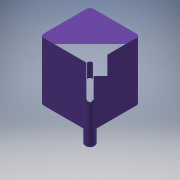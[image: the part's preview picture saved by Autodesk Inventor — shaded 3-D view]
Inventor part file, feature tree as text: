
AUTODESK INVENTOR PART (.ipt)
format: ipt  version: 2016 (Build 200138000, 138)  size: 137,216 bytes
history: native  units: mm
features: extrude x3, sketch x3, other x1, hole x1, chamfer x1, fillet x1
ambient origin geometry x8: Origin, YZ Plane, XZ Plane, XY Plane, X Axis, Y Axis, Z Axis, Center Point
bodies: Solid1 (feature_tree)
feature tree (10):
  other  "Fixture.ipt"
  extrude  "Extrusion1"  Depth=28.3mm
  hole  "Hole2"  [1 undecoded]
  sketch  "Sketch3"  dims[d3=51.0mm d4=0.0mm d12=2.0mm d13=0.0mm]
  extrude  "Extrusion2"  Depth=2.0mm TaperAngle=45.0deg
  extrude  "Extrusion3"  Depth=2.16mm
  chamfer  "Chamfer1"  Distance=10.0mm
  fillet  "Fillet1"  Radius=23.0mm
  sketch  "Sketch1"  dims[d0=28.3mm d2=22.0mm]
  sketch  "Sketch4"  dims[d15=20.0mm d16=0.0mm d17=0.6mm d18=2.0mm d19=45.0deg d20=2.16mm d21=10.0mm d22=23.0mm d23=2.5mm d24=6.0mm d25=4.0mm d26=2.0mm d27=90.0deg d28=8.0mm d29=20.594885mm d30=22.0mm d31=5.3mm]
note: 1 required parameter value undecoded (feature->parameter linkage not recoverable at this tier; creation-order binding heuristic only, values carry confidence <= 0.55)
